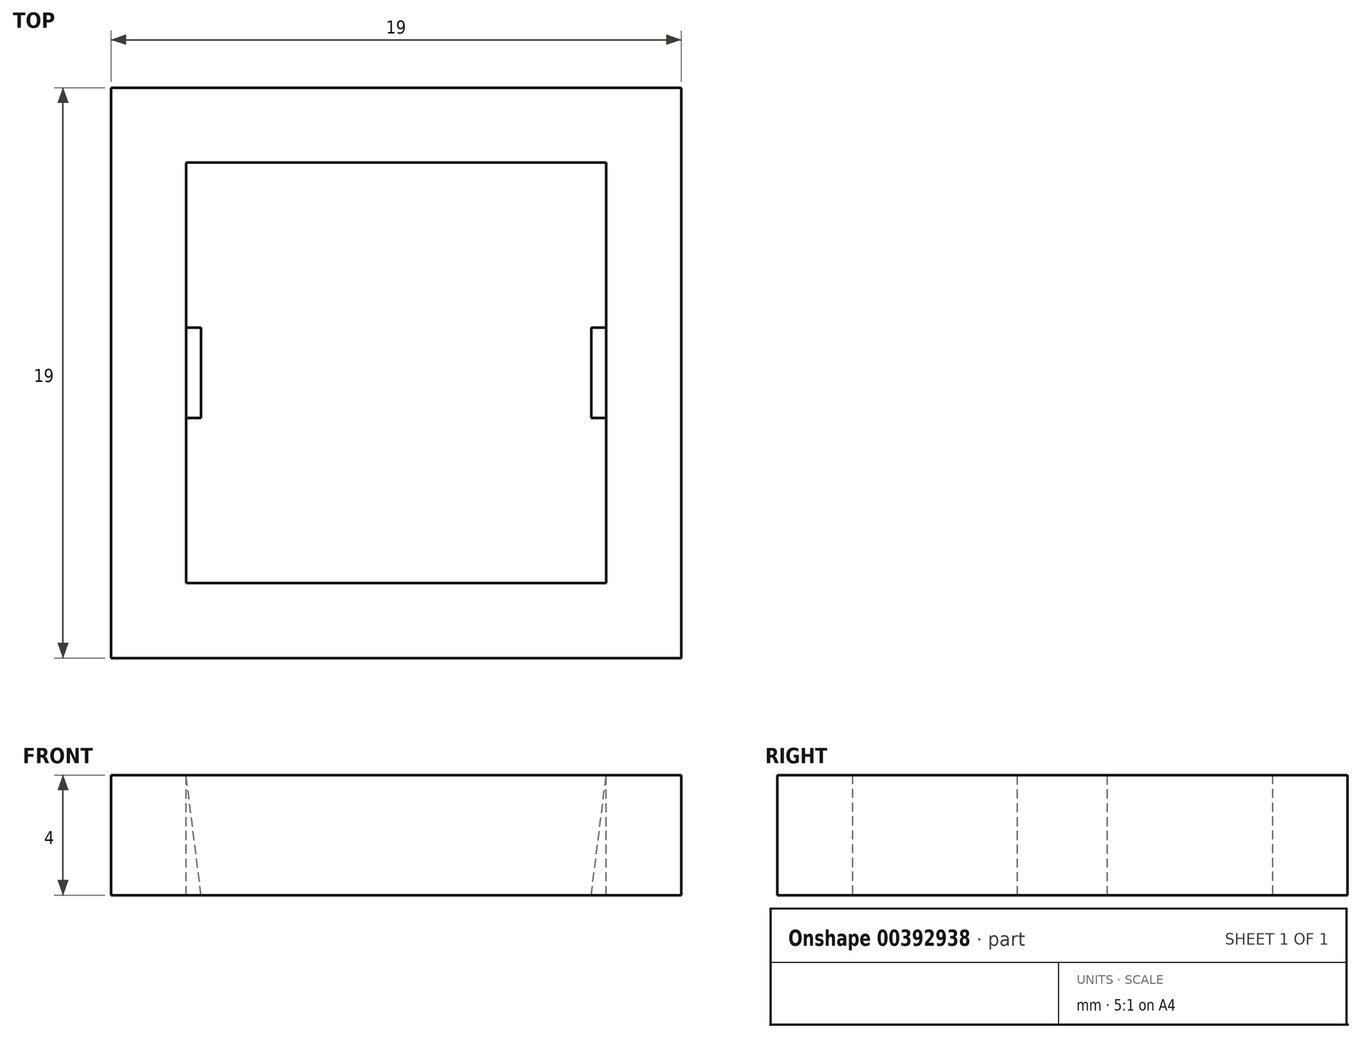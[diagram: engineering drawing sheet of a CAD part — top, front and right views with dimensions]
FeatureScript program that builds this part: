
annotation { "Feature Type Name" : "Feature", "Feature Type Description" : "" }
export const myFeature = defineFeature(function(context is Context, id is Id, definition is map)
    precondition{}
    {
        {
            var Q0;
            Q0=qCreatedBy(makeId("Top.planeOp"),FACE);
            var sketch = newSketch(context, id + "F0", { "sketchPlane" : qUnion([Q0])});
            skLineSegment(sketch, "E0.bottom", {"start": v(9.5, -9.5) * mm, "end": v(-9.5, -9.5) * mm});
            skLineSegment(sketch, "E0.top", {"start": v(9.5, 9.5) * mm, "end": v(-9.5, 9.5) * mm});
            skLineSegment(sketch, "E0.left", {"start": v(9.5, -9.5) * mm, "end": v(9.5, 9.5) * mm});
            skLineSegment(sketch, "E0.right", {"start": v(-9.5, -9.5) * mm, "end": v(-9.5, 9.5) * mm});
            skPoint(sketch, "E0.middle", {"position": v(0, 0) * mm});
            skLineSegment(sketch, "E1.bottom", {"start": v(7, -7) * mm, "end": v(-7, -7) * mm});
            skLineSegment(sketch, "E1.top", {"start": v(7, 7) * mm, "end": v(-7, 7) * mm});
            skLineSegment(sketch, "E1.left", {"start": v(7, -7) * mm, "end": v(7, 7) * mm});
            skLineSegment(sketch, "E1.right", {"start": v(-7, -7) * mm, "end": v(-7, 7) * mm});
            skSolve(sketch);
        }
        {
            var Q0;
            Q0=makeQuery(id+"F0.imprint","IMPRINT",FACE,{"disambiguationData":[TD([[makeQuery(id+"F0.imprint","IMPRINT",EDGE,{"derivedFrom":sQuery(id+"F0.wireOp",EDGE,"E0.bottom")}),-1.0]])]});
            extrude(context, id + "F1", {"entities" : qUnion([Q0]), "depth" : 4 * mm});
        }
        {
            var Q0;
            Q0=makeQuery(id+"F1.opExtrude","SWEPT_FACE",FACE,{"disambiguationData":[OSD([sQuery(id+"F0.wireOp",EDGE,"E1.right")])]});
            var sketch = newSketch(context, id + "F2", { "sketchPlane" : qUnion([Q0])});
            skLineSegment(sketch, "E2.bottom", {"start": v(-1.5, 0) * mm, "end": v(1.5, 0) * mm});
            skLineSegment(sketch, "E2.top", {"start": v(-1.5, 4) * mm, "end": v(1.5, 4) * mm});
            skLineSegment(sketch, "E2.left", {"start": v(-1.5, 0) * mm, "end": v(-1.5, 4) * mm});
            skLineSegment(sketch, "E2.right", {"start": v(1.5, 0) * mm, "end": v(1.5, 4) * mm});
            skPoint(sketch, "E2.middle", {"position": v(0, 2) * mm});
            skPoint(sketch, "E2.middle.positionSnap0", {"position": v(7, 2) * mm});
            skPoint(sketch, "E2.middle.positionSnap1", {"position": v(0, 4) * mm});
            skPoint(sketch, "E2.centerSnap0", {"position": v(7, 2) * mm});
            skPoint(sketch, "E2.centerSnap1", {"position": v(0, 4) * mm});
            skSolve(sketch);
        }
        {
            var Q0;
            Q0 = qSketchRegion(id + "F2", true);
            extrude(context, id + "F3", {"entities" : qUnion([Q0]), "operationType" : NewBodyOperationType.ADD, "depth" : 0.5 * mm});
        }
        {
            var Q0;
            Q0=makeQuery(id+"F3.opExtrude","SWEPT_FACE",FACE,{"disambiguationData":[OSD([sQuery(id+"F2.wireOp",EDGE,"E2.left")])]});
            var sketch = newSketch(context, id + "F4", { "sketchPlane" : qUnion([Q0])});
            skLineSegment(sketch, "E3", {"start": v(-7, 4) * mm, "end": v(-6.5, 0) * mm});
            skLineSegment(sketch, "E4", {"start": v(-6.5, 0) * mm, "end": v(-6.5, 4) * mm});
            skLineSegment(sketch, "E5", {"start": v(-6.5, 4) * mm, "end": v(-7, 4) * mm});
            skSolve(sketch);
        }
        {
            var Q0;
            Q0=makeQuery(id+"F4.imprint","IMPRINT",FACE,{"disambiguationData":[TD([[makeQuery(id+"F4.imprint","IMPRINT",EDGE,{"derivedFrom":sQuery(id+"F4.wireOp",EDGE,"E3")}),1.0]])]});
            extrude(context, id + "F5", {"entities" : qUnion([Q0]), "operationType" : NewBodyOperationType.REMOVE, "endBound" : BoundingType.UP_TO_NEXT, "oppositeDirection" : true, "depth" : 25.4 * mm});
        }
        {
            var Q0;
            Q0=makeQuery(id+"F1.opExtrude","SWEPT_FACE",FACE,{"disambiguationData":[OSD([sQuery(id+"F0.wireOp",EDGE,"E1.left")])]});
            var sketch = newSketch(context, id + "F6", { "sketchPlane" : qUnion([Q0])});
            skLineSegment(sketch, "E6.bottom", {"start": v(1.5, 0) * mm, "end": v(-1.5, 0) * mm});
            skLineSegment(sketch, "E6.top", {"start": v(1.5, 4) * mm, "end": v(-1.5, 4) * mm});
            skLineSegment(sketch, "E6.left", {"start": v(1.5, 0) * mm, "end": v(1.5, 4) * mm});
            skLineSegment(sketch, "E6.right", {"start": v(-1.5, 0) * mm, "end": v(-1.5, 4) * mm});
            skPoint(sketch, "E6.middle", {"position": v(0, 2) * mm});
            skPoint(sketch, "E6.middle.positionSnap0", {"position": v(-7, 2) * mm});
            skPoint(sketch, "E6.middle.positionSnap1", {"position": v(0, 4) * mm});
            skPoint(sketch, "E6.centerSnap0", {"position": v(-7, 2) * mm});
            skPoint(sketch, "E6.centerSnap1", {"position": v(0, 4) * mm});
            skSolve(sketch);
        }
        {
            var Q0;
            Q0 = qSketchRegion(id + "F6", true);
            extrude(context, id + "F7", {"entities" : qUnion([Q0]), "operationType" : NewBodyOperationType.ADD, "depth" : .5 * mm});
        }
        {
            var Q0;
            Q0=makeQuery(id+"F7.opExtrude","SWEPT_FACE",FACE,{"disambiguationData":[OSD([sQuery(id+"F6.wireOp",EDGE,"E6.left")])]});
            var sketch = newSketch(context, id + "F8", { "sketchPlane" : qUnion([Q0])});
            skLineSegment(sketch, "E7", {"start": v(6.5, 0) * mm, "end": v(7, 4) * mm});
            skLineSegment(sketch, "E8", {"start": v(7, 4) * mm, "end": v(6.5, 4) * mm});
            skLineSegment(sketch, "E9", {"start": v(6.5, 4) * mm, "end": v(6.5, 0) * mm});
            skSolve(sketch);
        }
        {
            var Q0;
            Q0=makeQuery(id+"F8.imprint","IMPRINT",FACE,{"disambiguationData":[TD([[makeQuery(id+"F8.imprint","IMPRINT",EDGE,{"derivedFrom":sQuery(id+"F8.wireOp",EDGE,"E7")}),1.0]])]});
            extrude(context, id + "F9", {"entities" : qUnion([Q0]), "operationType" : NewBodyOperationType.REMOVE, "endBound" : BoundingType.UP_TO_NEXT, "oppositeDirection" : true, "depth" : 25.4 * mm});
        }
    });
